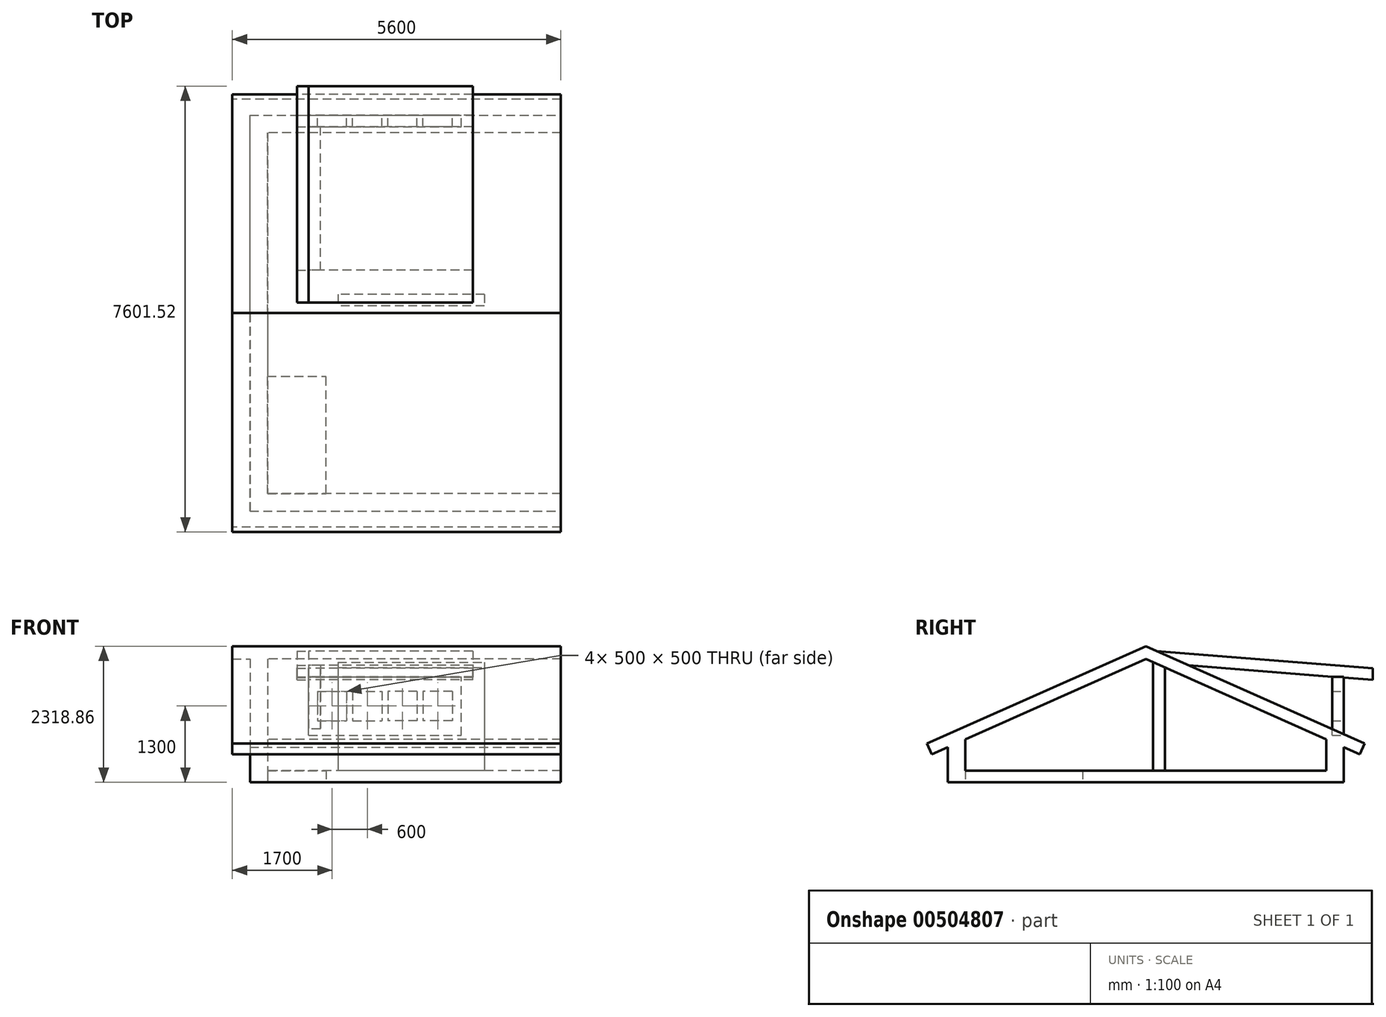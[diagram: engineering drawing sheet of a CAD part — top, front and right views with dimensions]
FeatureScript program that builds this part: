
annotation { "Feature Type Name" : "Feature", "Feature Type Description" : "" }
export const myFeature = defineFeature(function(context is Context, id is Id, definition is map)
    precondition{}
    {
        {
            var Q0;
            Q0=qCreatedBy(makeId("Top.planeOp"),FACE);
            var sketch = newSketch(context, id + "F0", { "sketchPlane" : qUnion([Q0])});
            skLineSegment(sketch, "E0.bottom", {"start": v(-7245.84, -3366.5) * mm, "end": v(-2245.84, -3366.5) * mm});
            skLineSegment(sketch, "E0.top", {"start": v(-7245.84, 3383.5) * mm, "end": v(-2245.84, 3383.5) * mm});
            skLineSegment(sketch, "E0.left", {"start": v(-7245.84, -3366.5) * mm, "end": v(-7245.84, 3383.5) * mm});
            skLineSegment(sketch, "E0.right", {"start": v(-2245.84, -3366.5) * mm, "end": v(-2245.84, 3383.5) * mm});
            skLineSegment(sketch, "E1.0", {"start": v(-6945.84, 3083.5) * mm, "end": v(-2245.84, 3083.5) * mm});
            skLineSegment(sketch, "E1.1", {"start": v(-6945.84, -3066.5) * mm, "end": v(-6945.84, 3083.5) * mm});
            skLineSegment(sketch, "E1.2", {"start": v(-6945.84, -3066.5) * mm, "end": v(-2245.84, -3066.5) * mm});
            skLineSegment(sketch, "E2.bottom", {"start": v(-6945.84, -3066.5) * mm, "end": v(-5945.84, -3066.5) * mm});
            skLineSegment(sketch, "E2.top", {"start": v(-6945.84, -1066.5) * mm, "end": v(-5945.84, -1066.5) * mm});
            skLineSegment(sketch, "E2.left", {"start": v(-6945.84, -3066.5) * mm, "end": v(-6945.84, -1066.5) * mm});
            skLineSegment(sketch, "E2.right", {"start": v(-5945.84, -3066.5) * mm, "end": v(-5945.84, -1066.5) * mm});
            skLineSegment(sketch, "E3.bottom", {"start": v(-3245.84, 331.29) * mm, "end": v(-5745.84, 331.29) * mm});
            skLineSegment(sketch, "E3.top", {"start": v(-3245.84, 131.29) * mm, "end": v(-5745.84, 131.29) * mm});
            skLineSegment(sketch, "E3.left", {"start": v(-3245.84, 331.29) * mm, "end": v(-3245.84, 131.29) * mm});
            skLineSegment(sketch, "E3.right", {"start": v(-5745.84, 331.29) * mm, "end": v(-5745.84, 131.29) * mm});
            skLineSegment(sketch, "E4", {"start": v(-3245.84, 331.29) * mm, "end": v(-2245.84, 331.29) * mm});
            skSolve(sketch);
        }
        {
            var Q0;
            {var subQ1=sQuery(id+"F0.wireOp",EDGE,"E1.0");Q0=makeQuery(id+"F0.imprint","IMPRINT",FACE,{"disambiguationData":[TD([[makeQuery(id+"F0.imprint","IMPRINT",EDGE,{"derivedFrom":subQ1}),-1.0]])]});}
            var Q1;
            {var subQ1=sQuery(id+"F0.wireOp",EDGE,"E0.bottom");Q1=makeQuery(id+"F0.imprint","IMPRINT",FACE,{"disambiguationData":[TD([[makeQuery(id+"F0.imprint","IMPRINT",EDGE,{"derivedFrom":subQ1}),1.0]])]});}
            extrude(context, id + "F1", {"entities" : qUnion([Q0, Q1]), "depth" : 200 * mm});
        }
        {
            var Q0;
            {var subQ1=sQuery(id+"F0.wireOp",EDGE,"E0.bottom");Q0=makeQuery(id+"F0.imprint","IMPRINT",FACE,{"disambiguationData":[TD([[makeQuery(id+"F0.imprint","IMPRINT",EDGE,{"derivedFrom":subQ1}),1.0]])]});}
            extrude(context, id + "F2", {"entities" : qUnion([Q0]), "operationType" : NewBodyOperationType.ADD, "depth" : 600 * mm});
        }
        {
            var Q0;
            {var subQ0=sQuery(id+"F0.wireOp",EDGE,"E0.left");Q0=makeQuery(id+"F2.boolean.opBoolean","MERGE",FACE,{"derivedFrom":[makeQuery(id+"F1.opExtrude","SWEPT_FACE",FACE,{"disambiguationData":[OSD([subQ0])]}),makeQuery(id+"F2.opExtrude","SWEPT_FACE",FACE,{"disambiguationData":[OSD([subQ0])]})]});}
            var sketch = newSketch(context, id + "F3", { "sketchPlane" : qUnion([Q0])});
            skLineSegment(sketch, "E5", {"start": v(-8.5, 600) * mm, "end": v(-8.5, 2100) * mm});
            skLineSegment(sketch, "E6", {"start": v(-8.5, 2100) * mm, "end": v(3366.5, 600) * mm});
            skLineSegment(sketch, "E7", {"start": v(-8.5, 2100) * mm, "end": v(-3383.5, 600) * mm});
            skLineSegment(sketch, "E8.0", {"start": v(-8.5, 2318.86) * mm, "end": v(-3464.73, 782.76) * mm});
            skLineSegment(sketch, "E8.1", {"start": v(-8.5, 2318.86) * mm, "end": v(3447.73, 782.76) * mm});
            skLineSegment(sketch, "E9", {"start": v(-3464.73, 782.76) * mm, "end": v(-3383.5, 600) * mm});
            skLineSegment(sketch, "E10", {"start": v(3447.73, 782.76) * mm, "end": v(3366.5, 600) * mm});
            skSolve(sketch);
        }
        {
            var Q0;
            Q0=makeQuery(id+"F3.imprint","IMPRINT",FACE,{"disambiguationData":[TD([[makeQuery(id+"F3.imprint","IMPRINT",EDGE,{"derivedFrom":sQuery(id+"F3.wireOp",EDGE,"E6")}),1.0]])]});
            extrude(context, id + "F4", {"entities" : qUnion([Q0]), "oppositeDirection" : true, "depth" : 5000 * mm});
        }
        {
            var Q0;
            Q0=makeQuery(id+"F4.opExtrude","SWEPT_FACE",FACE,{"disambiguationData":[OSD([sQuery(id+"F3.wireOp",EDGE,"E10")])]});
            extrude(context, id + "F5", {"entities" : qUnion([Q0]), "operationType" : NewBodyOperationType.ADD, "depth" : 300 * mm});
        }
        {
            var Q0;
            Q0=makeQuery(id+"F4.opExtrude","SWEPT_FACE",FACE,{"disambiguationData":[OSD([sQuery(id+"F3.wireOp",EDGE,"E9")])]});
            extrude(context, id + "F6", {"entities" : qUnion([Q0]), "operationType" : NewBodyOperationType.ADD, "depth" : 300 * mm});
        }
        {
            var Q0;
            Q0=makeQuery(id+"F2.opExtrude","CAP_FACE",FACE,{"disambiguationData":[OSD([sQuery(id+"F0.wireOp",EDGE,"E0.bottom"),sQuery(id+"F0.wireOp",EDGE,"E0.top"),sQuery(id+"F0.wireOp",EDGE,"E0.left"),sQuery(id+"F0.wireOp",EDGE,"E0.right"),sQuery(id+"F0.wireOp",EDGE,"E1.0"),sQuery(id+"F0.wireOp",EDGE,"E1.1"),sQuery(id+"F0.wireOp",EDGE,"E1.2"),sQuery(id+"F0.wireOp",EDGE,"E2.bottom"),sQuery(id+"F0.wireOp",EDGE,"E2.left")])],"isStart":false});
            extrude(context, id + "F7", {"entities" : qUnion([Q0]), "endBound" : BoundingType.UP_TO_NEXT, "depth" : 1500 * mm});
        }
        {
            var Q0;
            {var subQ0=sQuery(id+"F3.wireOp",EDGE,"E9");var subQ1=sQuery(id+"F3.wireOp",EDGE,"E10");Q0=makeQuery(id+"F6.boolean.opBoolean","MERGE",FACE,{"derivedFrom":[makeQuery(id+"F5.boolean.opBoolean","MERGE",FACE,{"derivedFrom":[makeQuery(id+"F4.opExtrude","CAP_FACE",FACE,{"disambiguationData":[OSD([sQuery(id+"F3.wireOp",EDGE,"E6"),sQuery(id+"F3.wireOp",EDGE,"E7"),sQuery(id+"F3.wireOp",EDGE,"E8.0"),sQuery(id+"F3.wireOp",EDGE,"E8.1"),subQ0,subQ1])],"isStart":true}),makeQuery(id+"F5.opExtrude","SWEPT_FACE",FACE,{"disambiguationData":[OSD([subQ1]),TDD([makeQuery(id+"F4.opExtrude","CAP_EDGE",EDGE,{"disambiguationData":[OSD([subQ1])],"isStart":true})])]})]}),makeQuery(id+"F6.opExtrude","SWEPT_FACE",FACE,{"disambiguationData":[OSD([subQ0]),TDD([makeQuery(id+"F4.opExtrude","CAP_EDGE",EDGE,{"disambiguationData":[OSD([subQ0])],"isStart":true})])]})]});}
            extrude(context, id + "F8", {"entities" : qUnion([Q0]), "operationType" : NewBodyOperationType.ADD, "depth" : 300 * mm});
        }
        {
            var Q0;
            {var subQ0=sQuery(id+"F3.wireOp",EDGE,"E9");var subQ1=sQuery(id+"F3.wireOp",EDGE,"E10");Q0=makeQuery(id+"F6.boolean.opBoolean","MERGE",FACE,{"derivedFrom":[makeQuery(id+"F5.boolean.opBoolean","MERGE",FACE,{"derivedFrom":[makeQuery(id+"F4.opExtrude","CAP_FACE",FACE,{"disambiguationData":[OSD([sQuery(id+"F3.wireOp",EDGE,"E6"),sQuery(id+"F3.wireOp",EDGE,"E7"),sQuery(id+"F3.wireOp",EDGE,"E8.0"),sQuery(id+"F3.wireOp",EDGE,"E8.1"),subQ0,subQ1])],"isStart":false}),makeQuery(id+"F5.opExtrude","SWEPT_FACE",FACE,{"disambiguationData":[OSD([subQ1]),TDD([makeQuery(id+"F4.opExtrude","CAP_EDGE",EDGE,{"disambiguationData":[OSD([subQ1])],"isStart":false})])]})]}),makeQuery(id+"F6.opExtrude","SWEPT_FACE",FACE,{"disambiguationData":[OSD([subQ0]),TDD([makeQuery(id+"F4.opExtrude","CAP_EDGE",EDGE,{"disambiguationData":[OSD([subQ0])],"isStart":false})])]})]});}
            extrude(context, id + "F9", {"entities" : qUnion([Q0]), "operationType" : NewBodyOperationType.ADD, "depth" : 300 * mm});
        }
        {
            var Q0;
            {var subQ0=sQuery(id+"F0.wireOp",EDGE,"E0.top");Q0=makeQuery(id+"F2.boolean.opBoolean","MERGE",FACE,{"derivedFrom":[makeQuery(id+"F1.opExtrude","SWEPT_FACE",FACE,{"disambiguationData":[OSD([subQ0])]}),makeQuery(id+"F2.opExtrude","SWEPT_FACE",FACE,{"disambiguationData":[OSD([subQ0])]})]});}
            var sketch = newSketch(context, id + "F10", { "sketchPlane" : qUnion([Q0])});
            skLineSegment(sketch, "E11.bottom", {"start": v(6245.84, 800) * mm, "end": v(3645.84, 800) * mm});
            skLineSegment(sketch, "E11.top", {"start": v(6245.84, 1800) * mm, "end": v(3645.84, 1800) * mm});
            skLineSegment(sketch, "E11.left", {"start": v(6245.84, 800) * mm, "end": v(6245.84, 1800) * mm});
            skLineSegment(sketch, "E11.right", {"start": v(3645.84, 800) * mm, "end": v(3645.84, 1800) * mm});
            skLineSegment(sketch, "E12", {"start": v(3645.84, 1300) * mm, "end": v(6245.84, 1300) * mm});
            skLineSegment(sketch, "E13", {"start": v(4945.84, 1800) * mm, "end": v(4945.84, 800) * mm});
            skPoint(sketch, "E14", {"position": v(4645.84, 1300) * mm});
            skPoint(sketch, "E15", {"position": v(4045.84, 1300) * mm});
            skLineSegment(sketch, "E16", {"start": v(4945.84, 1300) * mm, "end": v(4645.84, 1300) * mm});
            skLineSegment(sketch, "E17", {"start": v(4645.84, 1300) * mm, "end": v(4045.84, 1300) * mm});
            skLineSegment(sketch, "E18.bottom", {"start": v(3795.84, 1550) * mm, "end": v(4295.84, 1550) * mm});
            skLineSegment(sketch, "E18.top", {"start": v(3795.84, 1050) * mm, "end": v(4295.84, 1050) * mm});
            skLineSegment(sketch, "E18.left", {"start": v(3795.84, 1550) * mm, "end": v(3795.84, 1050) * mm});
            skLineSegment(sketch, "E18.right", {"start": v(4295.84, 1550) * mm, "end": v(4295.84, 1050) * mm});
            skLineSegment(sketch, "E19.bottom", {"start": v(4395.84, 1550) * mm, "end": v(4895.84, 1550) * mm});
            skLineSegment(sketch, "E19.top", {"start": v(4395.84, 1050) * mm, "end": v(4895.84, 1050) * mm});
            skLineSegment(sketch, "E19.left", {"start": v(4395.84, 1550) * mm, "end": v(4395.84, 1050) * mm});
            skLineSegment(sketch, "E19.right", {"start": v(4895.84, 1550) * mm, "end": v(4895.84, 1050) * mm});
            skPoint(sketch, "E20.MirrorP", {"position": v(5845.84, 1300) * mm});
            skPoint(sketch, "E21.MirrorP", {"position": v(5245.84, 1300) * mm});
            skLineSegment(sketch, "E22.MirrorCS", {"start": v(5245.84, 1300) * mm, "end": v(5845.84, 1300) * mm});
            skLineSegment(sketch, "E23.MirrorCS", {"start": v(6095.84, 1050) * mm, "end": v(5595.84, 1050) * mm});
            skLineSegment(sketch, "E24.MirrorCS", {"start": v(6095.84, 1550) * mm, "end": v(5595.84, 1550) * mm});
            skLineSegment(sketch, "E25.MirrorCS", {"start": v(5595.84, 1550) * mm, "end": v(5595.84, 1050) * mm});
            skLineSegment(sketch, "E26.MirrorCS", {"start": v(4995.84, 1550) * mm, "end": v(4995.84, 1050) * mm});
            skLineSegment(sketch, "E27.MirrorCS", {"start": v(5495.84, 1550) * mm, "end": v(5495.84, 1050) * mm});
            skLineSegment(sketch, "E28.MirrorCS", {"start": v(5495.84, 1050) * mm, "end": v(4995.84, 1050) * mm});
            skLineSegment(sketch, "E29.MirrorCS", {"start": v(6095.84, 1550) * mm, "end": v(6095.84, 1050) * mm});
            skLineSegment(sketch, "E30.MirrorCS", {"start": v(5495.84, 1550) * mm, "end": v(4995.84, 1550) * mm});
            skLineSegment(sketch, "E31.0", {"start": v(7245.84, 600) * mm, "end": v(2245.84, 600) * mm});
            skLineSegment(sketch, "E32", {"start": v(6245.84, 122.13) * mm, "end": v(7245.84, 122.13) * mm});
            skLineSegment(sketch, "E33", {"start": v(5912.85, 600) * mm, "end": v(5912.85, 800) * mm});
            skSolve(sketch);
        }
        {
            var Q0;
            {var subQ1=sQuery(id+"F10.wireOp",EDGE,"E18.bottom");Q0=makeQuery(id+"F10.imprint","IMPRINT",FACE,{"disambiguationData":[TD([[makeQuery(id+"F10.imprint","IMPRINT",EDGE,{"derivedFrom":subQ1}),1.0]])]});}
            var Q1;
            {var subQ7=sQuery(id+"F10.wireOp",EDGE,"E24.MirrorCS");Q1=makeQuery(id+"F10.imprint","IMPRINT",FACE,{"disambiguationData":[TD([[makeQuery(id+"F10.imprint","IMPRINT",EDGE,{"derivedFrom":subQ7}),-1.0]])]});}
            var Q2;
            {var subQ5=sQuery(id+"F10.wireOp",EDGE,"E23.MirrorCS");Q2=makeQuery(id+"F10.imprint","IMPRINT",FACE,{"disambiguationData":[TD([[makeQuery(id+"F10.imprint","IMPRINT",EDGE,{"derivedFrom":subQ5}),1.0]])]});}
            var Q3;
            {var subQ1=sQuery(id+"F10.wireOp",EDGE,"E18.top");Q3=makeQuery(id+"F10.imprint","IMPRINT",FACE,{"disambiguationData":[TD([[makeQuery(id+"F10.imprint","IMPRINT",EDGE,{"derivedFrom":subQ1}),-1.0]])]});}
            extrude(context, id + "F11", {"entities" : qUnion([Q0, Q1, Q2, Q3]), "oppositeDirection" : true, "depth" : 200 * mm});
        }
        {
            var Q0;
            Q0=makeQuery(id+"F11.opExtrude","SWEPT_FACE",FACE,{"disambiguationData":[OSD([sQuery(id+"F10.wireOp",EDGE,"E11.left")])]});
            var sketch = newSketch(context, id + "F12", { "sketchPlane" : qUnion([Q0])});
            skLineSegment(sketch, "E34.0", {"start": v(-8.5, 2318.86) * mm, "end": v(-3738.87, 660.92) * mm});
            skLineSegment(sketch, "E35", {"start": v(-3183.5, 1800) * mm, "end": v(-739.16, 1994.12) * mm});
            skLineSegment(sketch, "E36", {"start": v(-191.26, 2237.64) * mm, "end": v(-3879.65, 1944.71) * mm});
            skLineSegment(sketch, "E37", {"start": v(-3879.65, 1944.71) * mm, "end": v(-3879.65, 1744.71) * mm});
            skLineSegment(sketch, "E38", {"start": v(-3879.65, 1744.71) * mm, "end": v(-3183.5, 1800) * mm});
            skLineSegment(sketch, "E39", {"start": v(-8.5, 2318.86) * mm, "end": v(-191.26, 2237.64) * mm});
            skSolve(sketch);
        }
        {
            var Q0;
            {var subQ1=sQuery(id+"F12.wireOp",EDGE,"E35");Q0=makeQuery(id+"F12.imprint","IMPRINT",FACE,{"disambiguationData":[TD([[makeQuery(id+"F12.imprint","IMPRINT",EDGE,{"derivedFrom":subQ1}),1.0]])]});}
            extrude(context, id + "F13", {"entities" : qUnion([Q0]), "oppositeDirection" : true, "depth" : 2800 * mm});
        }
        {
            var Q0;
            {var subQ1=sQuery(id+"F12.wireOp",EDGE,"E35");Q0=makeQuery(id+"F12.imprint","IMPRINT",FACE,{"disambiguationData":[TD([[makeQuery(id+"F12.imprint","IMPRINT",EDGE,{"derivedFrom":subQ1}),1.0]])]});}
            extrude(context, id + "F14", {"entities" : qUnion([Q0]), "depth" : 200 * mm});
        }
        {
            var Q0;
            {var subQ0=sQuery(id+"F12.wireOp",EDGE,"E35");Q0=makeQuery(id+"F12.imprint","IMPRINT",FACE,{"disambiguationData":[TD([[makeQuery(id+"F12.imprint","IMPRINT",EDGE,{"derivedFrom":subQ0}),-1.0]])]});}
            extrude(context, id + "F15", {"entities" : qUnion([Q0]), "oppositeDirection" : true, "depth" : 200 * mm});
        }
        {
            var Q0;
            Q0=makeQuery(id+"F0.imprint","IMPRINT",FACE,{"disambiguationData":[TD([[makeQuery(id+"F0.imprint","IMPRINT",EDGE,{"derivedFrom":sQuery(id+"F0.wireOp",EDGE,"E3.bottom")}),1.0]])]});
            extrude(context, id + "F16", {"entities" : qUnion([Q0]), "operationType" : NewBodyOperationType.ADD, "depth" : 2100 * mm});
        }
    });
